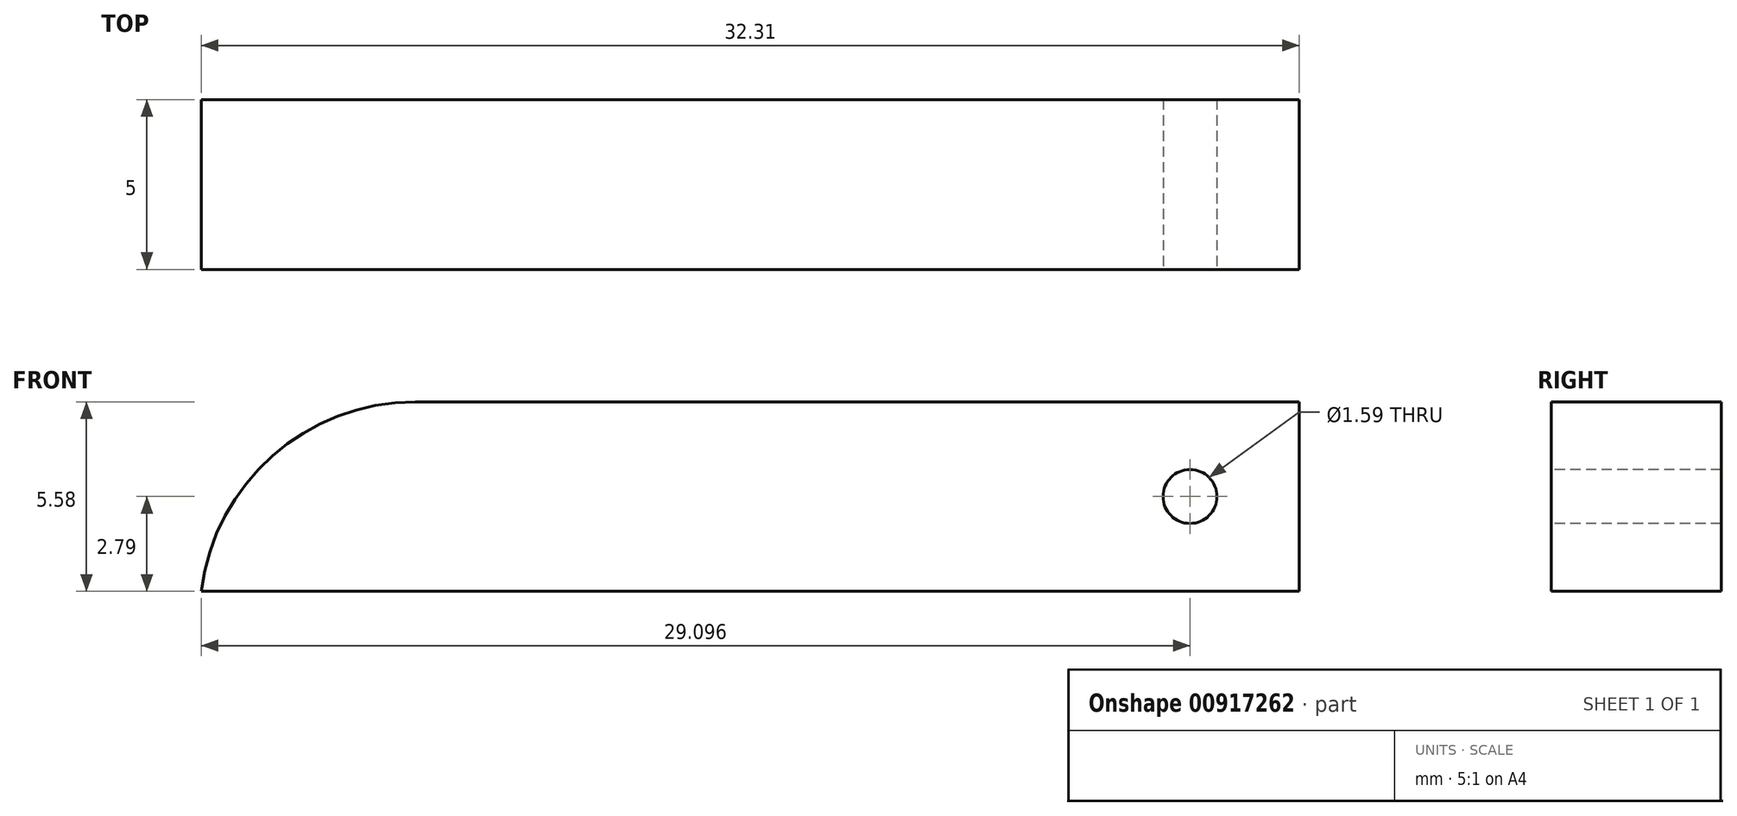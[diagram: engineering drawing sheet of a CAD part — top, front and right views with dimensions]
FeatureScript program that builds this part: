
annotation { "Feature Type Name" : "Feature", "Feature Type Description" : "" }
export const myFeature = defineFeature(function(context is Context, id is Id, definition is map)
    precondition{}
    {
        {
            var Q0;
            Q0=qCreatedBy(makeId("Front.planeOp"),FACE);
            var sketch = newSketch(context, id + "F0", { "sketchPlane" : qUnion([Q0])});
            skLineSegment(sketch, "E0.bottom", {"start": v(-16.18, -2.79) * mm, "end": v(16.18, -2.79) * mm});
            skLineSegment(sketch, "E0.top", {"start": v(-9.83, 2.79) * mm, "end": v(16.18, 2.79) * mm});
            skLineSegment(sketch, "E0.right", {"start": v(16.18, -2.79) * mm, "end": v(16.18, 2.79) * mm});
            skPoint(sketch, "E0.middle", {"position": v(0, 0) * mm});
            skPoint(sketch, "E1.visualSharp", {"position": v(-16.18, 2.79) * mm});
            skArc(sketch, "E1.filletArc", {"start": v(-9.83, 2.79) * mm, "mid": v(-14.04, 1.2) * mm, "end": v(-16.13, -2.79) * mm});
            skSolve(sketch);
        }
        {
            var Q0;
            Q0 = qSketchRegion(id + "F0", true);
            extrude(context, id + "F1", {"entities" : qUnion([Q0]), "endBound" : BoundingType.SYMMETRIC, "depth" : 5 * mm, "offsetDistance" : 25.4 * mm});
        }
        {
            var Q0;
            Q0=makeQuery(id+"F1.opExtrude","CAP_FACE",FACE,{"disambiguationData":[OSD([sQuery(id+"F0.wireOp",EDGE,"E0.bottom"),sQuery(id+"F0.wireOp",EDGE,"E0.top"),sQuery(id+"F0.wireOp",EDGE,"E0.right"),sQuery(id+"F0.wireOp",EDGE,"E1.filletArc")])],"isStart":false});
            var sketch = newSketch(context, id + "F2", { "sketchPlane" : qUnion([Q0])});
            skCircle(sketch, "E2", {"center": v(12.97, 0) * mm, "radius": 0.8 * mm});
            skSolve(sketch);
        }
        {
            var Q0;
            Q0 = qSketchRegion(id + "F2", true);
            extrude(context, id + "F3", {"entities" : qUnion([Q0]), "operationType" : NewBodyOperationType.REMOVE, "oppositeDirection" : true, "depth" : 25 * mm, "offsetDistance" : 25 * mm});
        }
    });
